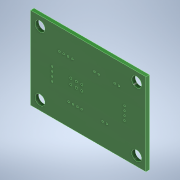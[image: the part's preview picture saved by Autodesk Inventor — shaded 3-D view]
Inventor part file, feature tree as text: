
AUTODESK INVENTOR PART (.ipt)
format: ipt  version: 2022 (Build 260153000, 153)  size: 181,760 bytes
history: native  units: mm
features: sketch x4, hole x3, extrude x1
ambient origin geometry x8: Origin, YZ Plane, XZ Plane, XY Plane, X Axis, Y Axis, Z Axis, Center Point
bodies: Solid1 (feature_tree)
feature tree (8):
  extrude  "Extrusion1"  Depth=38.1mm
  hole  "Hole1"  [1 undecoded]
  hole  "Hole2"  [1 undecoded]
  hole  "Hole3"  [1 undecoded]
  sketch  "Sketch1"  dims[d0=53.34mm d1=38.1mm]
  sketch  "Sketch2"  dims[d2=1.6mm d3=0.0mm d4=29.464mm]
  sketch  "Sketch3"  dims[d5=4.318mm d6=38.1mm]
  sketch  "Sketch4"  dims[d7=53.34mm d8=4.318mm d9=4.318mm d10=4.572mm d11=6.0mm d12=9.779mm d13=2.0mm d14=14.3117mm d15=8.0mm d16=20.594885mm d17=19.256mm d18=31.48mm d19=40.878mm d20=9.906mm d42=40.0mm d44=2.0mm d45=10.0mm d47=10.0mm d49=20.0mm d51=2.0mm d52=10.0mm d54=10.0mm d56=20.0mm d58=2.0mm d59=10.0mm d61=10.0mm d63=9.921mm d64=17.574mm d65=17.574mm d66=10.175mm d67=33.29mm d68=15.542mm d69=9.921mm d70=40.0mm d72=2.0mm d73=10.0mm d75=10.0mm d77=40.0mm d79=2.0mm d80=10.0mm d82=10.0mm d84=20.0mm d86=2.0mm d87=10.0mm d89=10.0mm d91=40.0mm d93=2.0mm d94=10.0mm d96=10.0mm d98=0.8mm d99=6.0mm d100=4.0mm d101=2.0mm d102=90.0deg d103=8.0mm d104=20.594885mm d105=20.579mm d106=18.557mm d107=30.0mm d109=2.54mm d110=20.0mm d112=2.54mm d115=1.0mm d116=6.0mm d117=4.0mm d118=2.0mm d119=90.0deg d120=8.0mm d121=20.594885mm]
note: 3 required parameter values undecoded (feature->parameter linkage not recoverable at this tier; creation-order binding heuristic only, values carry confidence <= 0.55)
